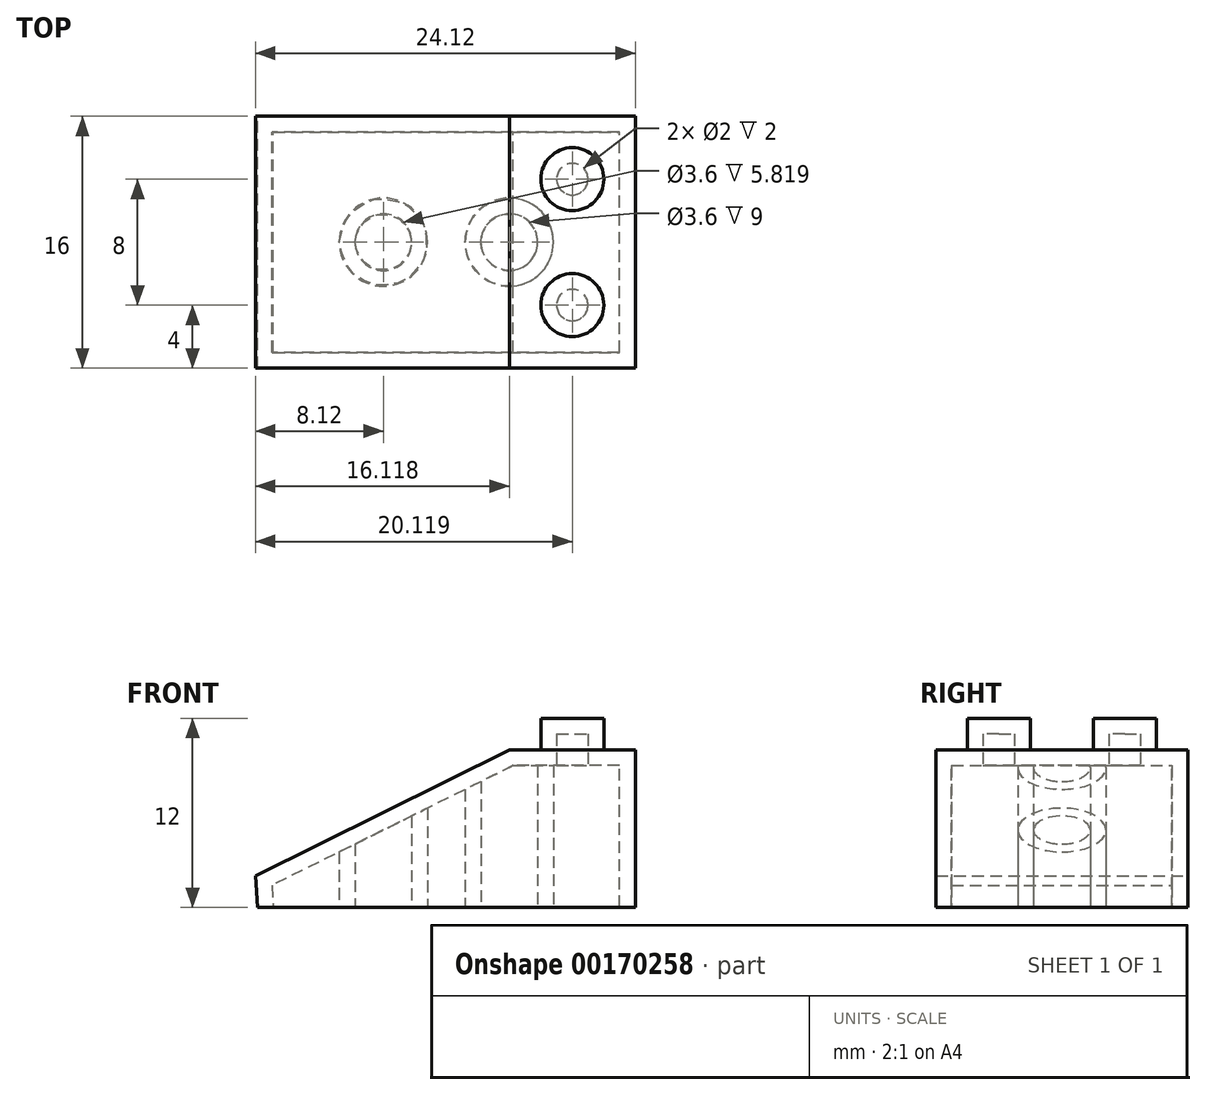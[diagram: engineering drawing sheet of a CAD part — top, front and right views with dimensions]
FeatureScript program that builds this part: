
annotation { "Feature Type Name" : "Feature", "Feature Type Description" : "" }
export const myFeature = defineFeature(function(context is Context, id is Id, definition is map)
    precondition{}
    {
        {
            var Q0;
            Q0=qCreatedBy(makeId("Front.planeOp"),FACE);
            var sketch = newSketch(context, id + "F0", { "sketchPlane" : qUnion([Q0])});
            skLineSegment(sketch, "E0", {"start": v(-22.15, -3.64) * mm, "end": v(1.85, -3.64) * mm});
            skLineSegment(sketch, "E1", {"start": v(1.85, -3.64) * mm, "end": v(1.85, 6.36) * mm});
            skLineSegment(sketch, "E2", {"start": v(1.85, 6.36) * mm, "end": v(-6.15, 6.36) * mm});
            skLineSegment(sketch, "E3", {"start": v(-6.15, 6.36) * mm, "end": v(-22.27, -1.65) * mm});
            skLineSegment(sketch, "E4", {"start": v(-22.27, -1.65) * mm, "end": v(-22.15, -3.64) * mm});
            skSolve(sketch);
        }
        {
            var Q0;
            Q0=makeQuery(id+"F0.imprint","IMPRINT",FACE,{"disambiguationData":[TD([[makeQuery(id+"F0.imprint","IMPRINT",EDGE,{"derivedFrom":sQuery(id+"F0.wireOp",EDGE,"E0")}),1.0]])]});
            extrude(context, id + "F1", {"entities" : qUnion([Q0]), "depth" : 16 * mm});
        }
        {
            var Q0;
            Q0=makeQuery(id+"F1.opExtrude","SWEPT_FACE",FACE,{"disambiguationData":[OSD([sQuery(id+"F0.wireOp",EDGE,"E2")])]});
            var sketch = newSketch(context, id + "F2", { "sketchPlane" : qUnion([Q0])});
            skCircle(sketch, "E5", {"center": v(-2.15, -4) * mm, "radius": 2 * mm});
            skLineSegment(sketch, "E6", {"start": v(1.85, -8) * mm, "end": v(-6.15, -8) * mm});
            skCircle(sketch, "E7.MirrorC", {"center": v(-2.15, -12) * mm, "radius": 2 * mm});
            skSolve(sketch);
        }
        {
            var Q0;
            Q0 = qSketchRegion(id + "F2", true);
            extrude(context, id + "F3", {"entities" : qUnion([Q0]), "operationType" : NewBodyOperationType.ADD, "depth" : 2 * mm});
        }
        {
            var Q0;
            Q0=makeQuery(id+"F1.opExtrude","SWEPT_FACE",FACE,{"disambiguationData":[OSD([sQuery(id+"F0.wireOp",EDGE,"E0")])]});
            shell(context, id + "F4", {"entities" : qUnion([Q0]), "thickness" : 1 * mm});
        }
        {
            var Q0;
            Q0=makeQuery(id+"F1.opExtrude","SWEPT_FACE",FACE,{"disambiguationData":[OSD([sQuery(id+"F0.wireOp",EDGE,"E0")])]});
            var sketch = newSketch(context, id + "F5", { "sketchPlane" : qUnion([Q0])});
            skCircle(sketch, "E8", {"center": v(-6.15, 8) * mm, "radius": 2.8 * mm});
            skCircle(sketch, "E9.0", {"center": v(-6.15, 8) * mm, "radius": 1.8 * mm});
            skCircle(sketch, "E10.MirrorC", {"center": v(-14.15, 8) * mm, "radius": 1.8 * mm});
            skCircle(sketch, "E11.MirrorC", {"center": v(-14.15, 8) * mm, "radius": 2.8 * mm});
            skSolve(sketch);
        }
        {
            var Q0;
            Q0 = qSketchRegion(id + "F5", true);
            extrude(context, id + "F6", {"entities" : qUnion([Q0]), "endBound" : BoundingType.UP_TO_NEXT, "oppositeDirection" : true, "depth" : 25 * mm});
        }
    });
